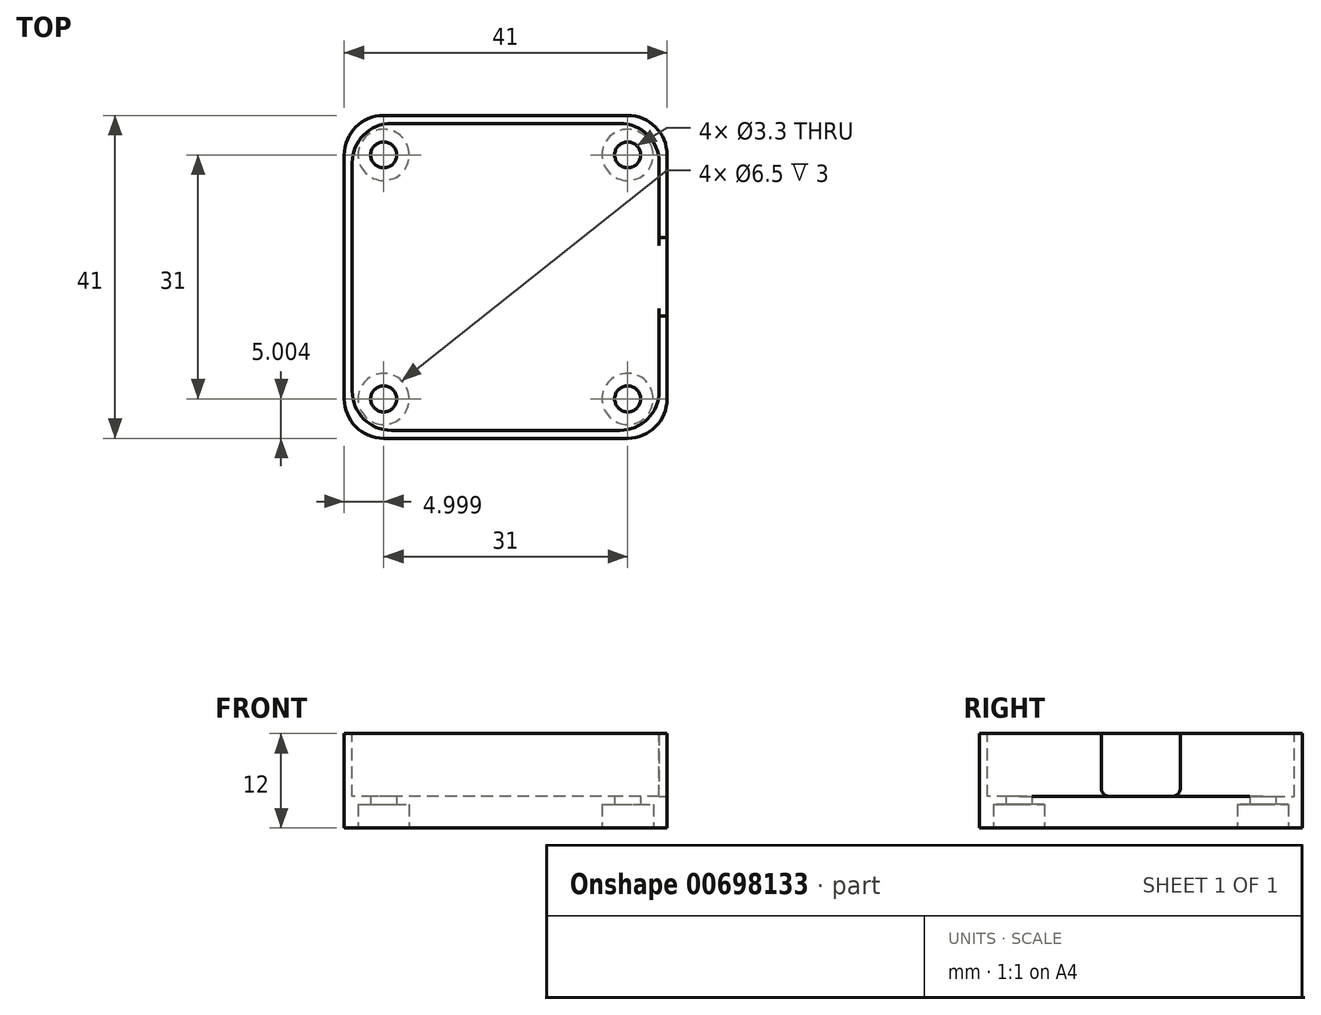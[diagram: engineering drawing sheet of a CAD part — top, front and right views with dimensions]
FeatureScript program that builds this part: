
annotation { "Feature Type Name" : "Feature", "Feature Type Description" : "" }
export const myFeature = defineFeature(function(context is Context, id is Id, definition is map)
    precondition{}
    {
        {
            var Q0;
            Q0=qCreatedBy(makeId("Top.planeOp"),FACE);
            var sketch = newSketch(context, id + "F0", { "sketchPlane" : qUnion([Q0])});
            skLineSegment(sketch, "E0.bottom", {"start": v(13.13, -16.19) * mm, "end": v(-27.87, -16.19) * mm});
            skLineSegment(sketch, "E0.top", {"start": v(13.13, 24.81) * mm, "end": v(-27.87, 24.81) * mm});
            skLineSegment(sketch, "E0.left", {"start": v(13.13, -16.19) * mm, "end": v(13.13, 24.81) * mm});
            skLineSegment(sketch, "E0.right", {"start": v(-27.87, -16.19) * mm, "end": v(-27.87, 24.81) * mm});
            skPoint(sketch, "E0.middle", {"position": v(-7.37, 4.31) * mm});
            skLineSegment(sketch, "E1", {"start": v(-56.7, 53.65) * mm, "end": v(-34.7, 31.65) * mm, "construction": true});
            skPoint(sketch, "E2", {"position": v(-22.87, 19.81) * mm});
            skPoint(sketch, "E3.1.0", {"position": v(-22.87, -11.19) * mm});
            skPoint(sketch, "E3.2.0", {"position": v(8.13, -11.19) * mm});
            skPoint(sketch, "E4.0.3.0", {"position": v(8.13, 19.81) * mm});
            skSolve(sketch);
        }
        {
            var Q0;
            Q0=makeQuery(id+"F0.imprint","IMPRINT",FACE,{"disambiguationData":[TD([[makeQuery(id+"F0.imprint","IMPRINT",EDGE,{"derivedFrom":sQuery(id+"F0.wireOp",EDGE,"E0.bottom")}),-1.0]])]});
            extrude(context, id + "F1", {"entities" : qUnion([Q0]), "depth" : 12 * mm, "offsetDistance" : 25 * mm});
        }
        {
            var Q0;
            Q0=sQuery(id+"F0.wireOp",VERTEX,"E4.0.3.0");
            var Q1;
            Q1=sQuery(id+"F0.wireOp",VERTEX,"E2");
            var Q2;
            Q2=sQuery(id+"F0.wireOp",VERTEX,"E3.1.0");
            var Q3;
            Q3=sQuery(id+"F0.wireOp",VERTEX,"E3.2.0");
            var Q4;
            Q4=makeQuery(id+"F1.opExtrude","SWEPT_BODY",BODY,{"disambiguationData":[OSD([sQuery(id+"F0.wireOp",EDGE,"E0.bottom"),sQuery(id+"F0.wireOp",EDGE,"E0.top"),sQuery(id+"F0.wireOp",EDGE,"E0.left"),sQuery(id+"F0.wireOp",EDGE,"E0.right")])]});
            hole(context, id + "F2", {"style" : HoleStyle.C_BORE, "endStyle" : HoleEndStyle.BLIND, "oppositeDirection" : true, "standardTappedOrClearance" : lookupTablePath({ "standard" : "ISO", "fit" : "Normal", "size" : "M3", "type" : "Clearance" }), "standardBlindInLast" : lookupTablePath({ "fit" : "Standard", "standard" : "ISO", "size" : "M3", "type" : "Clearance" }), "holeDiameter" : 3.3 * mm, "cBoreDiameter" : 6.5 * mm, "cBoreDepth" : 3 * mm, "majorDiameter" : 5 * mm, "holeDepth" : 20 * mm, "isTappedThrough" : true, "tappedDepth" : 12 * mm, "tapClearance" : 3, "startFromSketch" : true, "locations" : qUnion([Q0, Q1, Q2, Q3]), "scope" : qUnion([Q4])});
        }
        {
            var Q0;
            Q0=makeQuery(id+"F1.opExtrude","CAP_FACE",FACE,{"disambiguationData":[OSD([sQuery(id+"F0.wireOp",EDGE,"E0.bottom"),sQuery(id+"F0.wireOp",EDGE,"E0.top"),sQuery(id+"F0.wireOp",EDGE,"E0.left"),sQuery(id+"F0.wireOp",EDGE,"E0.right")])],"isStart":false});
            var sketch = newSketch(context, id + "F3", { "sketchPlane" : qUnion([Q0])});
            skPoint(sketch, "E5.0", {"position": v(-7.37, 4.31) * mm});
            skLineSegment(sketch, "E6.bottom", {"start": v(12.13, -15.19) * mm, "end": v(-26.87, -15.19) * mm});
            skLineSegment(sketch, "E6.top", {"start": v(12.13, 23.81) * mm, "end": v(-26.87, 23.81) * mm});
            skLineSegment(sketch, "E6.left", {"start": v(12.13, -15.19) * mm, "end": v(12.13, 23.81) * mm});
            skLineSegment(sketch, "E6.right", {"start": v(-26.87, -15.19) * mm, "end": v(-26.87, 23.81) * mm});
            skSolve(sketch);
        }
        {
            var Q0;
            Q0 = qSketchRegion(id + "F3", true);
            extrude(context, id + "F4", {"entities" : qUnion([Q0]), "operationType" : NewBodyOperationType.REMOVE, "oppositeDirection" : true, "depth" : 8 * mm, "offsetDistance" : 25 * mm});
        }
        {
            var Q0;
            Q0=makeQuery(id+"F1.opExtrude","SWEPT_EDGE",EDGE,{"disambiguationData":[OSD([sQuery(id+"F0.wireOp",EDGE,"E0.bottom"),sQuery(id+"F0.wireOp",EDGE,"E0.left")])]});
            var Q1;
            Q1=makeQuery(id+"F4.boolean.opBoolean","COPY",EDGE,{"derivedFrom":makeQuery(id+"F4.opExtrude","SWEPT_EDGE",EDGE,{"disambiguationData":[OSD([sQuery(id+"F3.wireOp",EDGE,"E6.bottom"),sQuery(id+"F3.wireOp",EDGE,"E6.left")])]})});
            var Q2;
            Q2=makeQuery(id+"F1.opExtrude","SWEPT_EDGE",EDGE,{"disambiguationData":[OSD([sQuery(id+"F0.wireOp",EDGE,"E0.bottom"),sQuery(id+"F0.wireOp",EDGE,"E0.right")])]});
            var Q3;
            Q3=makeQuery(id+"F4.boolean.opBoolean","COPY",EDGE,{"derivedFrom":makeQuery(id+"F4.opExtrude","SWEPT_EDGE",EDGE,{"disambiguationData":[OSD([sQuery(id+"F3.wireOp",EDGE,"E6.bottom"),sQuery(id+"F3.wireOp",EDGE,"E6.right")])]})});
            var Q4;
            Q4=makeQuery(id+"F1.opExtrude","SWEPT_EDGE",EDGE,{"disambiguationData":[OSD([sQuery(id+"F0.wireOp",EDGE,"E0.top"),sQuery(id+"F0.wireOp",EDGE,"E0.right")])]});
            var Q5;
            Q5=makeQuery(id+"F4.boolean.opBoolean","COPY",EDGE,{"derivedFrom":makeQuery(id+"F4.opExtrude","SWEPT_EDGE",EDGE,{"disambiguationData":[OSD([sQuery(id+"F3.wireOp",EDGE,"E6.top"),sQuery(id+"F3.wireOp",EDGE,"E6.right")])]})});
            var Q6;
            Q6=makeQuery(id+"F1.opExtrude","SWEPT_EDGE",EDGE,{"disambiguationData":[OSD([sQuery(id+"F0.wireOp",EDGE,"E0.top"),sQuery(id+"F0.wireOp",EDGE,"E0.left")])]});
            var Q7;
            Q7=makeQuery(id+"F4.boolean.opBoolean","COPY",EDGE,{"derivedFrom":makeQuery(id+"F4.opExtrude","SWEPT_EDGE",EDGE,{"disambiguationData":[OSD([sQuery(id+"F3.wireOp",EDGE,"E6.top"),sQuery(id+"F3.wireOp",EDGE,"E6.left")])]})});
            fillet(context, id + "F5", {"entities" : qUnion([Q0, Q1, Q2, Q3, Q4, Q5, Q6, Q7]), "radius" : 5 * mm, "tangentPropagation" : true, "allowEdgeOverflow" : false});
        }
        {
            var Q0;
            Q0=makeQuery(id+"F1.opExtrude","SWEPT_FACE",FACE,{"disambiguationData":[OSD([sQuery(id+"F0.wireOp",EDGE,"E0.left")])]});
            var sketch = newSketch(context, id + "F6", { "sketchPlane" : qUnion([Q0])});
            skLineSegment(sketch, "E7.bottom", {"start": v(9.31, 4) * mm, "end": v(-0.69, 4) * mm});
            skLineSegment(sketch, "E7.top", {"start": v(9.31, 20) * mm, "end": v(-0.69, 20) * mm});
            skLineSegment(sketch, "E7.left", {"start": v(9.31, 4) * mm, "end": v(9.31, 20) * mm});
            skLineSegment(sketch, "E7.right", {"start": v(-0.69, 4) * mm, "end": v(-0.69, 20) * mm});
            skPoint(sketch, "E7.middle", {"position": v(4.31, 12) * mm});
            skSolve(sketch);
        }
        {
            var Q0;
            {var subQ0=sQuery(id+"F6.wireOp",EDGE,"E7.bottom");Q0=makeQuery(id+"F6.imprint","IMPRINT",FACE,{"disambiguationData":[TD([[makeQuery(id+"F6.imprint","IMPRINT",EDGE,{"derivedFrom":subQ0}),-1.0]])]});}
            var Q1;
            Q1=makeQuery(id+"F4.boolean.opBoolean","COPY",FACE,{"derivedFrom":makeQuery(id+"F4.opExtrude","SWEPT_FACE",FACE,{"disambiguationData":[OSD([sQuery(id+"F3.wireOp",EDGE,"E6.left")])]})});
            extrude(context, id + "F7", {"entities" : qUnion([Q0]), "operationType" : NewBodyOperationType.REMOVE, "endBound" : BoundingType.UP_TO_SURFACE, "oppositeDirection" : true, "depth" : 25 * mm, "endBoundEntityFace" : qUnion([Q1]), "offsetDistance" : 25 * mm});
        }
        {
            var Q0;
            Q0=makeQuery(id+"F7.boolean.opBoolean","COPY",EDGE,{"derivedFrom":makeQuery(id+"F7.opExtrude","SWEPT_EDGE",EDGE,{"disambiguationData":[OSD([sQuery(id+"F6.wireOp",EDGE,"E7.bottom"),sQuery(id+"F6.wireOp",EDGE,"E7.left")])]})});
            var Q1;
            Q1=makeQuery(id+"F7.boolean.opBoolean","COPY",EDGE,{"derivedFrom":makeQuery(id+"F7.opExtrude","SWEPT_EDGE",EDGE,{"disambiguationData":[OSD([sQuery(id+"F6.wireOp",EDGE,"E7.bottom"),sQuery(id+"F6.wireOp",EDGE,"E7.right")])]})});
            fillet(context, id + "F8", {"entities" : qUnion([Q0, Q1]), "radius" : 1 * mm, "tangentPropagation" : true, "allowEdgeOverflow" : false});
        }
    });
